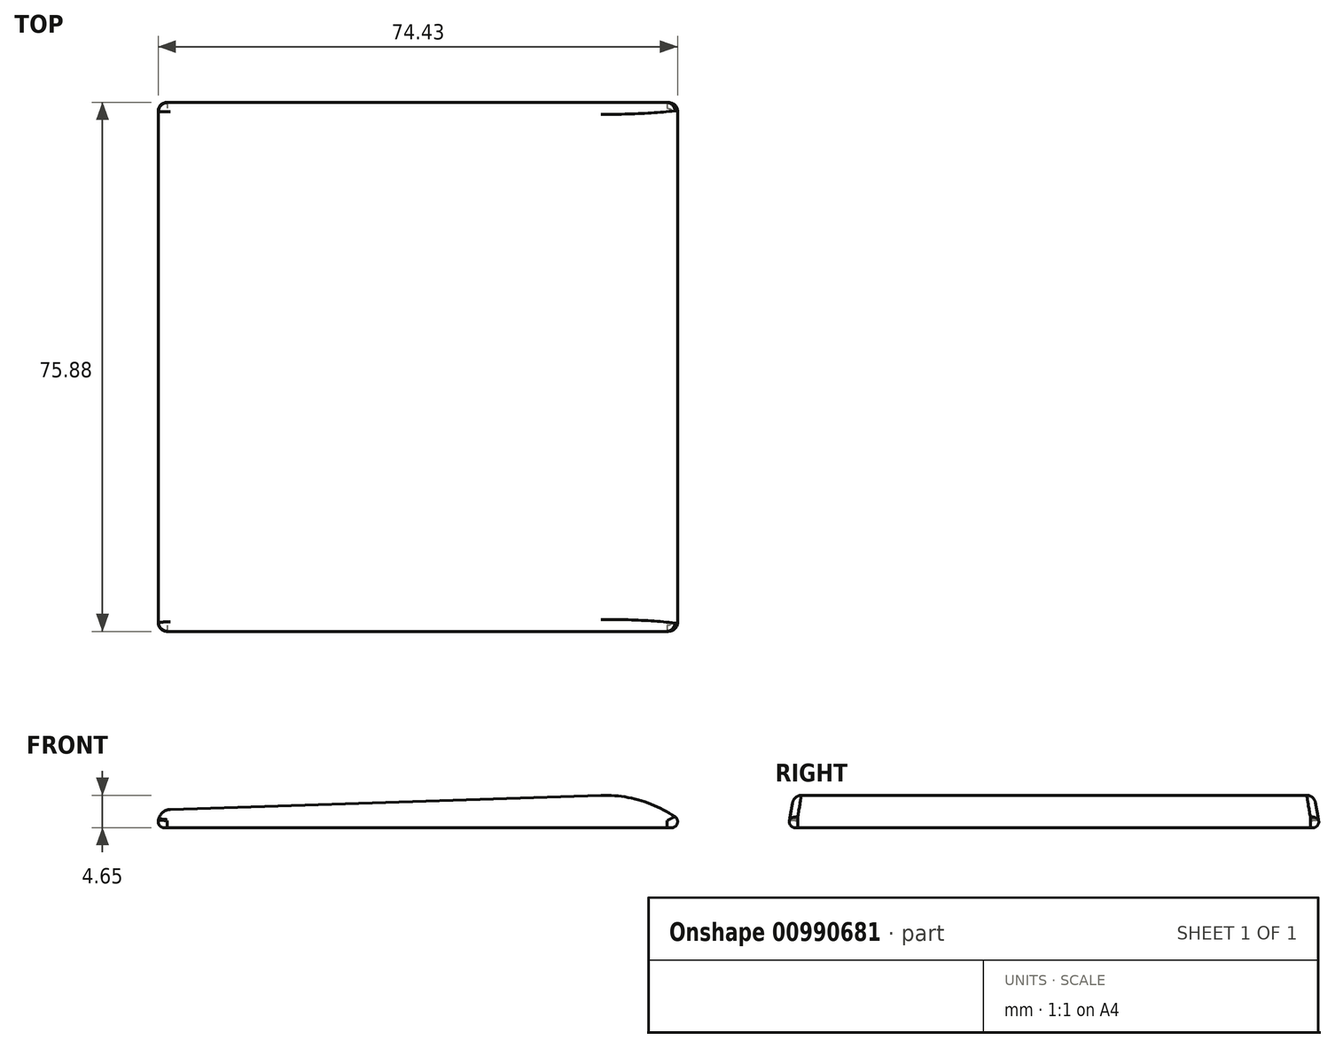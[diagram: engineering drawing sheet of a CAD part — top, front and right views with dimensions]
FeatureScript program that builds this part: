
annotation { "Feature Type Name" : "Feature", "Feature Type Description" : "" }
export const myFeature = defineFeature(function(context is Context, id is Id, definition is map)
    precondition{}
    {
        {
            var Q0;
            Q0=qCreatedBy(makeId("Top.planeOp"),FACE);
            var sketch = newSketch(context, id + "F0", { "sketchPlane" : qUnion([Q0])});
            skLineSegment(sketch, "E0.bottom", {"start": v(-37.96, 38.1) * mm, "end": v(38.24, 38.1) * mm});
            skLineSegment(sketch, "E0.top", {"start": v(-37.96, -38.1) * mm, "end": v(38.24, -38.1) * mm});
            skLineSegment(sketch, "E0.left", {"start": v(-37.96, 38.1) * mm, "end": v(-37.96, -38.1) * mm});
            skLineSegment(sketch, "E0.right", {"start": v(38.24, 38.1) * mm, "end": v(38.24, -38.1) * mm});
            skSolve(sketch);
        }
        {
            var Q0;
            Q0=makeQuery(id+"F0.imprint","IMPRINT",FACE,{"disambiguationData":[TD([[makeQuery(id+"F0.imprint","IMPRINT",EDGE,{"derivedFrom":sQuery(id+"F0.wireOp",EDGE,"E0.bottom")}),-1.0]])]});
            extrude(context, id + "F1", {"entities" : qUnion([Q0]), "depth" : 5.08 * mm, "offsetDistance" : 25.4 * mm, "hasDraft" : true, "draftAngle" : 10 * degree, "draftPullDirection" : true});
        }
        {
            var Q0;
            Q0=makeQuery(id+"F1.opExtrude","CAP_EDGE",EDGE,{"disambiguationData":[OSD([sQuery(id+"F0.wireOp",EDGE,"E0.left")])],"isStart":false});
            chamfer(context, id + "F2", {"entities" : qUnion([Q0]), "chamferType" : ChamferType.TWO_OFFSETS, "width1" : 76.2 * mm, "oppositeDirection" : false, "width2" : 2.54 * mm, "tangentPropagation" : true});
        }
        {
            var Q0;
            {var subQ0=sQuery(id+"F0.wireOp",EDGE,"E0.left");Q0=makeQuery(id+"F2.opChamfer","BLEND_EDGE",EDGE,{"blendedFrom":[makeQuery(id+"F1.opExtrude","CAP_EDGE",EDGE,{"disambiguationData":[OSD([subQ0])],"isStart":false}),makeQuery(id+"F1.opExtrude","SWEPT_FACE",FACE,{"disambiguationData":[OSD([subQ0])]})],"blendedInto":[makeQuery(id+"F1.opExtrude","SWEPT_FACE",FACE,{"disambiguationData":[OSD([subQ0])]})]});}
            fillet(context, id + "F3", {"entities" : qUnion([Q0]), "radius" : 1.78 * mm, "tangentPropagation" : true, "allowEdgeOverflow" : false});
        }
        {
            var Q0;
            Q0=makeQuery(id+"F2.opChamfer","BLEND_EDGE",EDGE,{"blendedFrom":[makeQuery(id+"F1.opExtrude","CAP_EDGE",EDGE,{"disambiguationData":[OSD([sQuery(id+"F0.wireOp",EDGE,"E0.left")])],"isStart":false}),makeQuery(id+"F1.opExtrude","SWEPT_FACE",FACE,{"disambiguationData":[OSD([sQuery(id+"F0.wireOp",EDGE,"E0.right")])]})],"blendedInto":[makeQuery(id+"F1.opExtrude","SWEPT_FACE",FACE,{"disambiguationData":[OSD([sQuery(id+"F0.wireOp",EDGE,"E0.right")])]})]});
            fillet(context, id + "F4", {"entities" : qUnion([Q0]), "radius" : 17.78 * mm, "tangentPropagation" : true, "allowEdgeOverflow" : false});
        }
        {
            var Q0;
            Q0=makeQuery(id+"F2.opChamfer","BLEND_EDGE",EDGE,{"blendedFrom":[makeQuery(id+"F1.opExtrude","CAP_EDGE",EDGE,{"disambiguationData":[OSD([sQuery(id+"F0.wireOp",EDGE,"E0.left")])],"isStart":false}),makeQuery(id+"F1.opExtrude","SWEPT_FACE",FACE,{"disambiguationData":[OSD([sQuery(id+"F0.wireOp",EDGE,"E0.top")])]})],"blendedInto":[makeQuery(id+"F1.opExtrude","SWEPT_FACE",FACE,{"disambiguationData":[OSD([sQuery(id+"F0.wireOp",EDGE,"E0.top")])]})]});
            var Q1;
            {var subQ0=sQuery(id+"F0.wireOp",EDGE,"E0.left");Q1=makeQuery(id+"F3.opFillet","BLEND_EDGE",EDGE,{"blendedFrom":[makeQuery(id+"F2.opChamfer","BLEND_EDGE",EDGE,{"blendedFrom":[makeQuery(id+"F1.opExtrude","CAP_EDGE",EDGE,{"disambiguationData":[OSD([subQ0])],"isStart":false}),makeQuery(id+"F1.opExtrude","SWEPT_FACE",FACE,{"disambiguationData":[OSD([subQ0])]})],"blendedInto":[makeQuery(id+"F1.opExtrude","SWEPT_FACE",FACE,{"disambiguationData":[OSD([subQ0])]})]}),makeQuery(id+"F1.opExtrude","SWEPT_FACE",FACE,{"disambiguationData":[OSD([sQuery(id+"F0.wireOp",EDGE,"E0.top")])]})],"blendedInto":[makeQuery(id+"F1.opExtrude","SWEPT_FACE",FACE,{"disambiguationData":[OSD([sQuery(id+"F0.wireOp",EDGE,"E0.top")])]})]});}
            var Q2;
            Q2=makeQuery(id+"F2.opChamfer","BLEND_EDGE",EDGE,{"blendedFrom":[makeQuery(id+"F1.opExtrude","CAP_EDGE",EDGE,{"disambiguationData":[OSD([sQuery(id+"F0.wireOp",EDGE,"E0.left")])],"isStart":false}),makeQuery(id+"F1.opExtrude","SWEPT_FACE",FACE,{"disambiguationData":[OSD([sQuery(id+"F0.wireOp",EDGE,"E0.bottom")])]})],"blendedInto":[makeQuery(id+"F1.opExtrude","SWEPT_FACE",FACE,{"disambiguationData":[OSD([sQuery(id+"F0.wireOp",EDGE,"E0.bottom")])]})]});
            fillet(context, id + "F5", {"entities" : qUnion([Q0, Q1, Q2]), "radius" : 1.27 * mm, "tangentPropagation" : true, "allowEdgeOverflow" : false});
        }
        {
            var Q0;
            Q0=makeQuery(id+"F1.opExtrude","CAP_EDGE",EDGE,{"disambiguationData":[OSD([sQuery(id+"F0.wireOp",EDGE,"E0.bottom")])],"isStart":true});
            var Q1;
            Q1=makeQuery(id+"F1.opExtrude","CAP_EDGE",EDGE,{"disambiguationData":[OSD([sQuery(id+"F0.wireOp",EDGE,"E0.left")])],"isStart":true});
            var Q2;
            {var subQ0=sQuery(id+"F0.wireOp",EDGE,"E0.right");var subQ1=sQuery(id+"F0.wireOp",EDGE,"E0.left");Q2=makeQuery(id+"F4.opFillet","BLEND_EDGE",EDGE,{"blendedFrom":[makeQuery(id+"F2.opChamfer","BLEND_EDGE",EDGE,{"blendedFrom":[makeQuery(id+"F1.opExtrude","CAP_EDGE",EDGE,{"disambiguationData":[OSD([subQ1])],"isStart":false}),makeQuery(id+"F1.opExtrude","SWEPT_FACE",FACE,{"disambiguationData":[OSD([subQ0])]})],"blendedInto":[makeQuery(id+"F1.opExtrude","SWEPT_FACE",FACE,{"disambiguationData":[OSD([subQ0])]})]}),makeQuery(id+"F1.opExtrude","CAP_FACE",FACE,{"disambiguationData":[OSD([sQuery(id+"F0.wireOp",EDGE,"E0.bottom"),sQuery(id+"F0.wireOp",EDGE,"E0.top"),subQ1,subQ0])],"isStart":true})],"blendedInto":[makeQuery(id+"F1.opExtrude","CAP_FACE",FACE,{"disambiguationData":[OSD([sQuery(id+"F0.wireOp",EDGE,"E0.bottom"),sQuery(id+"F0.wireOp",EDGE,"E0.top"),subQ1,subQ0])],"isStart":true})]});}
            var Q3;
            Q3=makeQuery(id+"F1.opExtrude","CAP_EDGE",EDGE,{"disambiguationData":[OSD([sQuery(id+"F0.wireOp",EDGE,"E0.top")])],"isStart":true});
            var Q4;
            {var subQ0=sQuery(id+"F0.wireOp",EDGE,"E0.right");var subQ1=sQuery(id+"F0.wireOp",EDGE,"E0.left");var subQ2=sQuery(id+"F0.wireOp",EDGE,"E0.top");Q4=makeQuery(id+"F5.opFillet","BLEND_EDGE",EDGE,{"blendedFrom":[makeQuery(id+"F4.opFillet","BLEND_EDGE",EDGE,{"blendedFrom":[makeQuery(id+"F2.opChamfer","BLEND_EDGE",EDGE,{"blendedFrom":[makeQuery(id+"F1.opExtrude","CAP_EDGE",EDGE,{"disambiguationData":[OSD([subQ1])],"isStart":false}),makeQuery(id+"F1.opExtrude","SWEPT_FACE",FACE,{"disambiguationData":[OSD([subQ0])]})],"blendedInto":[makeQuery(id+"F1.opExtrude","SWEPT_FACE",FACE,{"disambiguationData":[OSD([subQ0])]})]}),makeQuery(id+"F1.opExtrude","SWEPT_FACE",FACE,{"disambiguationData":[OSD([subQ2])]})],"blendedInto":[makeQuery(id+"F1.opExtrude","SWEPT_FACE",FACE,{"disambiguationData":[OSD([subQ2])]})]}),makeQuery(id+"F1.opExtrude","CAP_FACE",FACE,{"disambiguationData":[OSD([sQuery(id+"F0.wireOp",EDGE,"E0.bottom"),subQ2,subQ1,subQ0])],"isStart":true})],"blendedInto":[makeQuery(id+"F1.opExtrude","CAP_FACE",FACE,{"disambiguationData":[OSD([sQuery(id+"F0.wireOp",EDGE,"E0.bottom"),subQ2,subQ1,subQ0])],"isStart":true})]});}
            var Q5;
            {var subQ0=sQuery(id+"F0.wireOp",EDGE,"E0.left");var subQ1=sQuery(id+"F0.wireOp",EDGE,"E0.top");Q5=makeQuery(id+"F5.opFillet","BLEND_EDGE",EDGE,{"blendedFrom":[makeQuery(id+"F1.opExtrude","SWEPT_EDGE",EDGE,{"disambiguationData":[OSD([subQ1,subQ0])]}),makeQuery(id+"F1.opExtrude","CAP_FACE",FACE,{"disambiguationData":[OSD([sQuery(id+"F0.wireOp",EDGE,"E0.bottom"),subQ1,subQ0,sQuery(id+"F0.wireOp",EDGE,"E0.right")])],"isStart":true})],"blendedInto":[makeQuery(id+"F1.opExtrude","CAP_FACE",FACE,{"disambiguationData":[OSD([sQuery(id+"F0.wireOp",EDGE,"E0.bottom"),subQ1,subQ0,sQuery(id+"F0.wireOp",EDGE,"E0.right")])],"isStart":true})]});}
            var Q6;
            {var subQ0=sQuery(id+"F0.wireOp",EDGE,"E0.left");var subQ1=sQuery(id+"F0.wireOp",EDGE,"E0.bottom");Q6=makeQuery(id+"F5.opFillet","BLEND_EDGE",EDGE,{"blendedFrom":[makeQuery(id+"F1.opExtrude","SWEPT_EDGE",EDGE,{"disambiguationData":[OSD([subQ1,subQ0])]}),makeQuery(id+"F1.opExtrude","CAP_FACE",FACE,{"disambiguationData":[OSD([subQ1,sQuery(id+"F0.wireOp",EDGE,"E0.top"),subQ0,sQuery(id+"F0.wireOp",EDGE,"E0.right")])],"isStart":true})],"blendedInto":[makeQuery(id+"F1.opExtrude","CAP_FACE",FACE,{"disambiguationData":[OSD([subQ1,sQuery(id+"F0.wireOp",EDGE,"E0.top"),subQ0,sQuery(id+"F0.wireOp",EDGE,"E0.right")])],"isStart":true})]});}
            var Q7;
            {var subQ0=sQuery(id+"F0.wireOp",EDGE,"E0.right");var subQ1=sQuery(id+"F0.wireOp",EDGE,"E0.left");var subQ2=sQuery(id+"F0.wireOp",EDGE,"E0.bottom");Q7=makeQuery(id+"F5.opFillet","BLEND_EDGE",EDGE,{"blendedFrom":[makeQuery(id+"F4.opFillet","BLEND_EDGE",EDGE,{"blendedFrom":[makeQuery(id+"F2.opChamfer","BLEND_EDGE",EDGE,{"blendedFrom":[makeQuery(id+"F1.opExtrude","CAP_EDGE",EDGE,{"disambiguationData":[OSD([subQ1])],"isStart":false}),makeQuery(id+"F1.opExtrude","SWEPT_FACE",FACE,{"disambiguationData":[OSD([subQ0])]})],"blendedInto":[makeQuery(id+"F1.opExtrude","SWEPT_FACE",FACE,{"disambiguationData":[OSD([subQ0])]})]}),makeQuery(id+"F1.opExtrude","SWEPT_FACE",FACE,{"disambiguationData":[OSD([subQ2])]})],"blendedInto":[makeQuery(id+"F1.opExtrude","SWEPT_FACE",FACE,{"disambiguationData":[OSD([subQ2])]})]}),makeQuery(id+"F1.opExtrude","CAP_FACE",FACE,{"disambiguationData":[OSD([subQ2,sQuery(id+"F0.wireOp",EDGE,"E0.top"),subQ1,subQ0])],"isStart":true})],"blendedInto":[makeQuery(id+"F1.opExtrude","CAP_FACE",FACE,{"disambiguationData":[OSD([subQ2,sQuery(id+"F0.wireOp",EDGE,"E0.top"),subQ1,subQ0])],"isStart":true})]});}
            fillet(context, id + "F6", {"entities" : qUnion([Q0, Q1, Q2, Q3, Q4, Q5, Q6, Q7]), "radius" : 0.86 * mm, "tangentPropagation" : true, "allowEdgeOverflow" : false});
        }
    });
